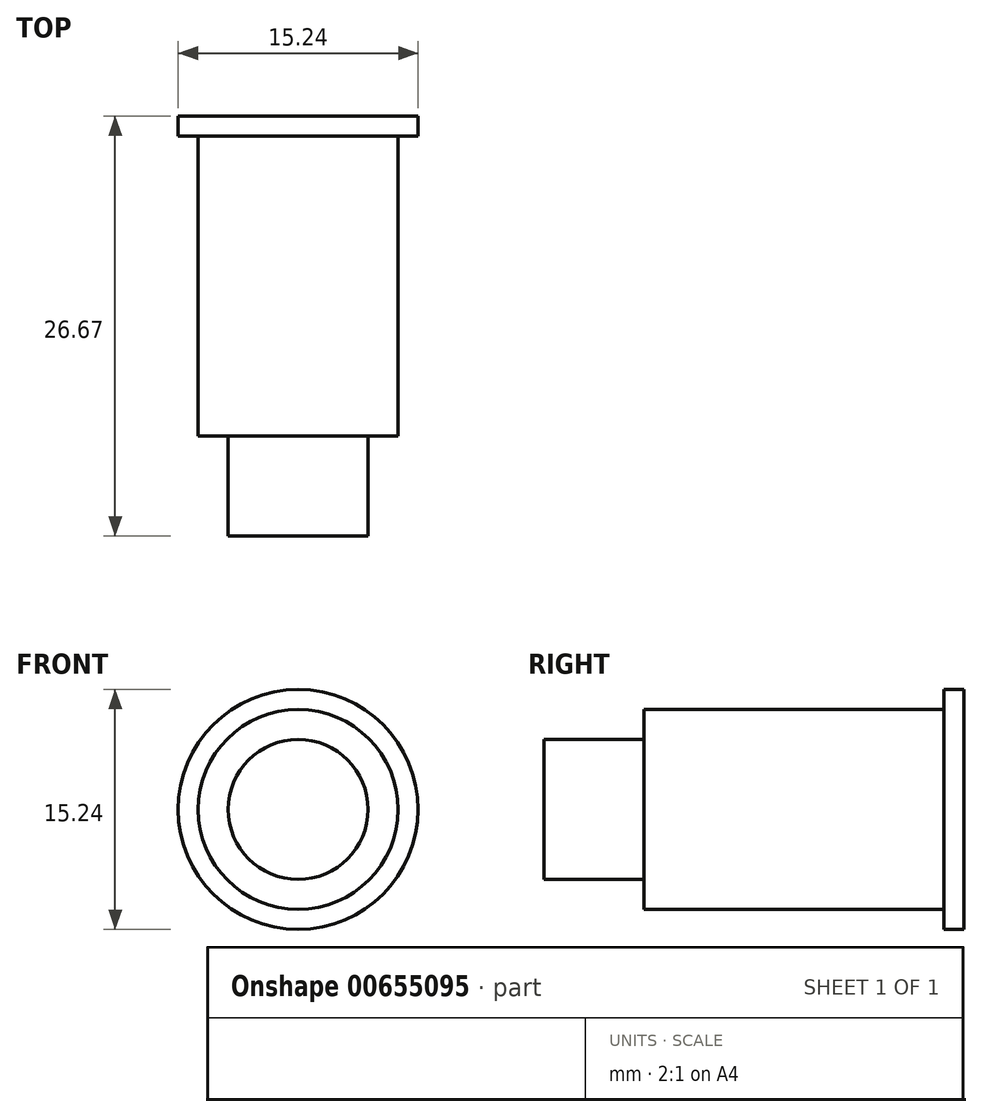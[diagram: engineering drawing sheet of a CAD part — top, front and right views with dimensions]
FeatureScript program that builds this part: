
annotation { "Feature Type Name" : "Feature", "Feature Type Description" : "" }
export const myFeature = defineFeature(function(context is Context, id is Id, definition is map)
    precondition{}
    {
        {
            var Q0;
            Q0=qCreatedBy(makeId("Front.planeOp"),FACE);
            var sketch = newSketch(context, id + "F0", { "sketchPlane" : qUnion([Q0])});
            skCircle(sketch, "E0", {"center": v(0, 0) * mm, "radius": 6.35 * mm});
            skSolve(sketch);
        }
        {
            var Q0;
            Q0 = qSketchRegion(id + "F0", true);
            extrude(context, id + "F1", {"entities" : qUnion([Q0]), "depth" : 19.05 * mm, "offsetDistance" : 25.4 * mm});
        }
        {
            var Q0;
            Q0=makeQuery(id+"F1.opExtrude","CAP_FACE",FACE,{"disambiguationData":[OSD([sQuery(id+"F0.wireOp",EDGE,"E0")])],"isStart":true});
            var sketch = newSketch(context, id + "F2", { "sketchPlane" : qUnion([Q0])});
            skCircle(sketch, "E1", {"center": v(0, 0) * mm, "radius": 7.62 * mm});
            skSolve(sketch);
        }
        {
            var Q0;
            Q0 = qSketchRegion(id + "F2", true);
            extrude(context, id + "F3", {"entities" : qUnion([Q0]), "operationType" : NewBodyOperationType.ADD, "depth" : 1.27 * mm, "offsetDistance" : 25.4 * mm});
        }
        {
            var Q0;
            Q0=makeQuery(id+"F1.opExtrude","CAP_FACE",FACE,{"disambiguationData":[OSD([sQuery(id+"F0.wireOp",EDGE,"E0")])],"isStart":false});
            var sketch = newSketch(context, id + "F4", { "sketchPlane" : qUnion([Q0])});
            skCircle(sketch, "E2", {"center": v(0, 0) * mm, "radius": 4.45 * mm});
            skSolve(sketch);
        }
        {
            var Q0;
            Q0 = qSketchRegion(id + "F4", true);
            extrude(context, id + "F5", {"entities" : qUnion([Q0]), "operationType" : NewBodyOperationType.ADD, "depth" : 6.35 * mm, "offsetDistance" : 25.4 * mm});
        }
    });
